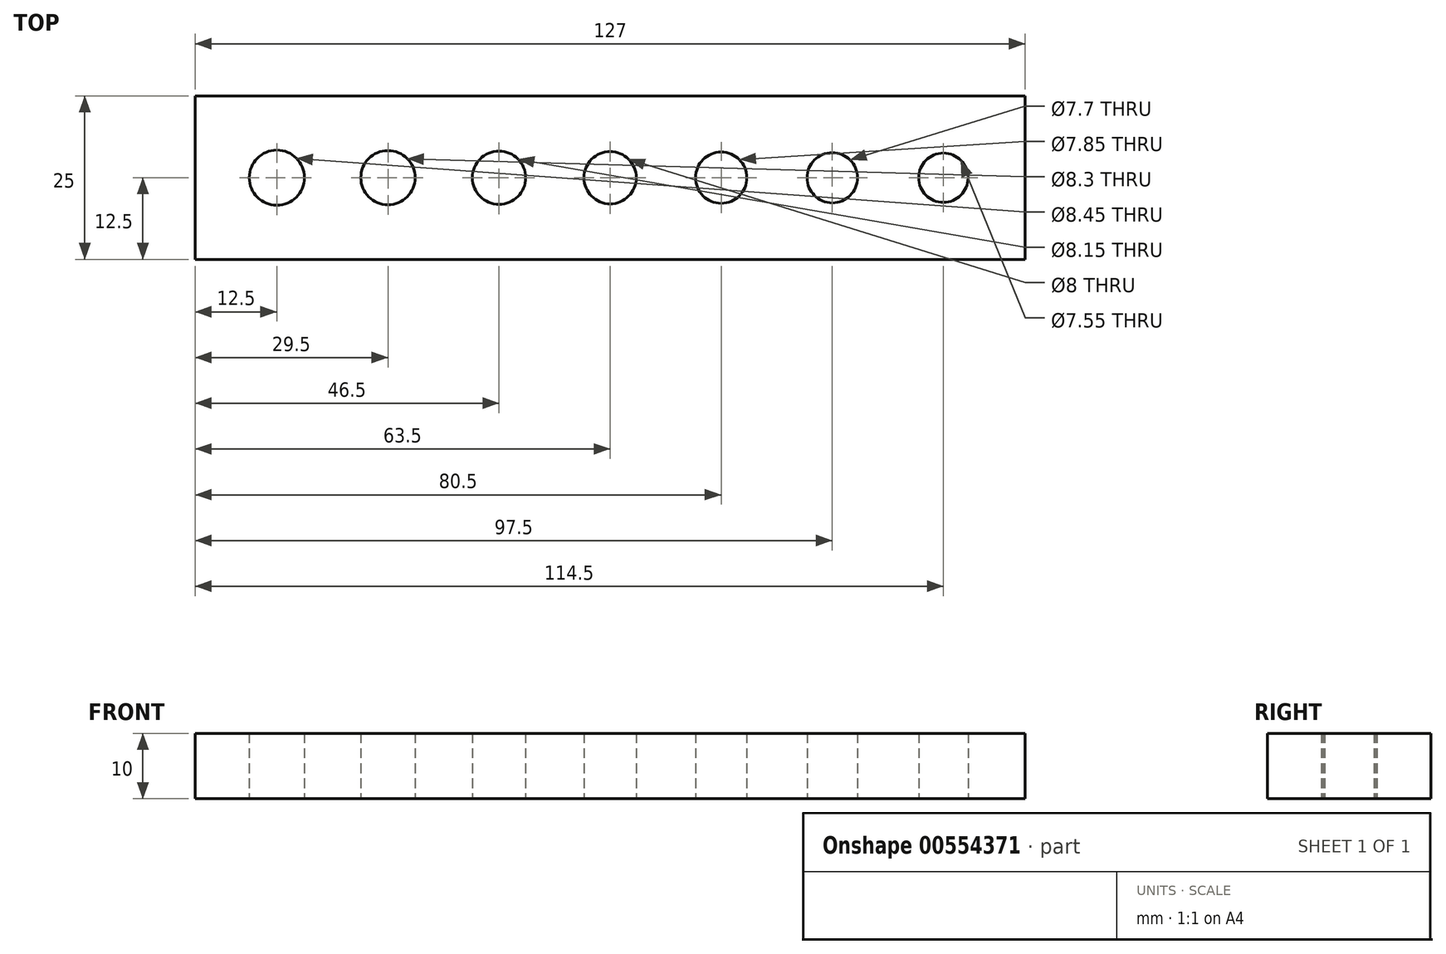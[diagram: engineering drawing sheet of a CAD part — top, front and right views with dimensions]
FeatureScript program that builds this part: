
annotation { "Feature Type Name" : "Feature", "Feature Type Description" : "" }
export const myFeature = defineFeature(function(context is Context, id is Id, definition is map)
    precondition{}
    {
        {
            var Q0;
            Q0=qCreatedBy(makeId("Top.planeOp"),FACE);
            var sketch = newSketch(context, id + "F0", { "sketchPlane" : qUnion([Q0])});
            skCircle(sketch, "E0", {"center": v(0, 0) * mm, "radius": 4 * mm});
            skLineSegment(sketch, "E1.bottom", {"start": v(63.5, 12.5) * mm, "end": v(-63.5, 12.5) * mm});
            skLineSegment(sketch, "E1.top", {"start": v(63.5, -12.5) * mm, "end": v(-63.5, -12.5) * mm});
            skLineSegment(sketch, "E1.left", {"start": v(63.5, 12.5) * mm, "end": v(63.5, -12.5) * mm});
            skLineSegment(sketch, "E1.right", {"start": v(-63.5, 12.5) * mm, "end": v(-63.5, -12.5) * mm});
            skPoint(sketch, "E2", {"position": v(51, 0) * mm});
            skPoint(sketch, "E3.1.0.0", {"position": v(34, 0) * mm});
            skPoint(sketch, "E3.2.0.0", {"position": v(17, 0) * mm});
            skPoint(sketch, "E3.4.0.0", {"position": v(-17, 0) * mm});
            skPoint(sketch, "E3.5.0.0", {"position": v(-34, 0) * mm});
            skPoint(sketch, "E3.6.0.0", {"position": v(-51, 0) * mm});
            skLineSegment(sketch, "E3.direction1", {"start": v(51, 0) * mm, "end": v(34, 0) * mm, "construction": true});
            skCircle(sketch, "E4", {"center": v(-17, 0) * mm, "radius": 4.08 * mm});
            skCircle(sketch, "E5", {"center": v(-51, 0) * mm, "radius": 4.22 * mm});
            skCircle(sketch, "E6", {"center": v(-34, 0) * mm, "radius": 4.15 * mm});
            skCircle(sketch, "E7", {"center": v(17, 0) * mm, "radius": 3.92 * mm});
            skCircle(sketch, "E8", {"center": v(34, 0) * mm, "radius": 3.85 * mm});
            skCircle(sketch, "E9", {"center": v(51, 0) * mm, "radius": 3.78 * mm});
            skCircle(sketch, "E10", {"center": v(-51, 0) * mm, "radius": 12.5 * mm, "construction": true});
            skSolve(sketch);
        }
        {
            var Q0;
            Q0 = qSketchRegion(id + "F0", true);
            extrude(context, id + "F1", {"entities" : qUnion([Q0]), "depth" : 10 * mm, "offsetDistance" : 25 * mm});
        }
    });
